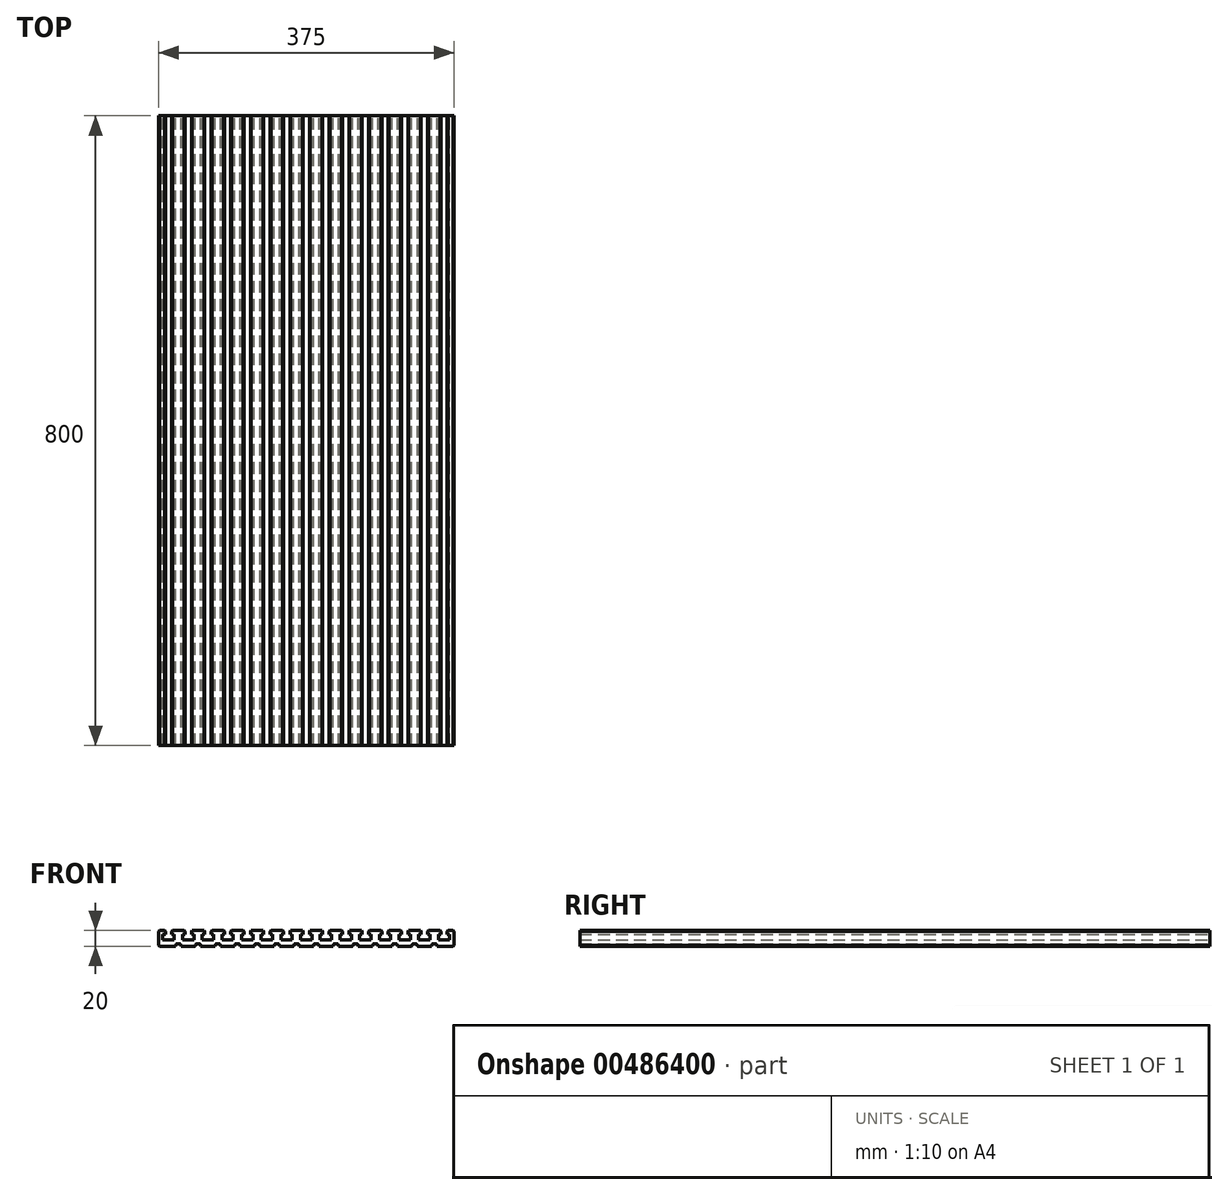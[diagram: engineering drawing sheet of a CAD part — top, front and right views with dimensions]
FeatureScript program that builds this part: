
annotation { "Feature Type Name" : "Feature", "Feature Type Description" : "" }
export const myFeature = defineFeature(function(context is Context, id is Id, definition is map)
    precondition{}
    {
        {
            var Q0;
            Q0=qCreatedBy(makeId("Front.planeOp"),FACE);
            var sketch = newSketch(context, id + "F0", { "sketchPlane" : qUnion([Q0])});
            skLineSegment(sketch, "E0", {"start": v(-186.5, -10) * mm, "end": v(-187.5, -9) * mm});
            skLineSegment(sketch, "E1", {"start": v(-187.5, -9) * mm, "end": v(-187.5, 9) * mm});
            skLineSegment(sketch, "E2", {"start": v(-187.5, 9) * mm, "end": v(-186.5, 10) * mm});
            skLineSegment(sketch, "E3", {"start": v(-186.5, 10) * mm, "end": v(-180.05, 10) * mm});
            skLineSegment(sketch, "E4", {"start": v(-179.05, 9) * mm, "end": v(-180.05, 10) * mm});
            skLineSegment(sketch, "E5", {"start": v(-179.05, 5) * mm, "end": v(-179.05, 9) * mm});
            skLineSegment(sketch, "E6", {"start": v(-182.25, 5) * mm, "end": v(-179.05, 5) * mm});
            skLineSegment(sketch, "E7", {"start": v(-182.25, -2) * mm, "end": v(-182.25, 5) * mm});
            skLineSegment(sketch, "E8", {"start": v(-167.75, -2) * mm, "end": v(-182.25, -2) * mm});
            skLineSegment(sketch, "E9", {"start": v(-167.75, 5) * mm, "end": v(-167.75, -2) * mm});
            skLineSegment(sketch, "E10", {"start": v(-170.95, 5) * mm, "end": v(-167.75, 5) * mm});
            skLineSegment(sketch, "E11", {"start": v(-170.95, 9) * mm, "end": v(-170.95, 5) * mm});
            skLineSegment(sketch, "E12", {"start": v(-169.95, 10) * mm, "end": v(-170.95, 9) * mm});
            skLineSegment(sketch, "E13", {"start": v(-169.95, 10) * mm, "end": v(-155.05, 10) * mm});
            skLineSegment(sketch, "E14", {"start": v(-154.05, 9) * mm, "end": v(-155.05, 10) * mm});
            skLineSegment(sketch, "E15", {"start": v(-154.05, 5) * mm, "end": v(-154.05, 9) * mm});
            skLineSegment(sketch, "E16", {"start": v(-157.25, 5) * mm, "end": v(-154.05, 5) * mm});
            skLineSegment(sketch, "E17", {"start": v(-157.25, -2) * mm, "end": v(-157.25, 5) * mm});
            skLineSegment(sketch, "E18", {"start": v(-142.75, -2) * mm, "end": v(-157.25, -2) * mm});
            skLineSegment(sketch, "E19", {"start": v(-142.75, 5) * mm, "end": v(-142.75, -2) * mm});
            skLineSegment(sketch, "E20", {"start": v(-145.95, 5) * mm, "end": v(-142.75, 5) * mm});
            skLineSegment(sketch, "E21", {"start": v(-145.95, 9) * mm, "end": v(-145.95, 5) * mm});
            skLineSegment(sketch, "E22", {"start": v(-144.95, 10) * mm, "end": v(-145.95, 9) * mm});
            skLineSegment(sketch, "E23", {"start": v(-144.95, 10) * mm, "end": v(-130.05, 10) * mm});
            skLineSegment(sketch, "E24", {"start": v(-129.05, 9) * mm, "end": v(-130.05, 10) * mm});
            skLineSegment(sketch, "E25", {"start": v(-129.05, 5) * mm, "end": v(-129.05, 9) * mm});
            skLineSegment(sketch, "E26", {"start": v(-132.25, 5) * mm, "end": v(-129.05, 5) * mm});
            skLineSegment(sketch, "E27", {"start": v(-132.25, -2) * mm, "end": v(-132.25, 5) * mm});
            skLineSegment(sketch, "E28", {"start": v(-117.75, -2) * mm, "end": v(-132.25, -2) * mm});
            skLineSegment(sketch, "E29", {"start": v(-117.75, 5) * mm, "end": v(-117.75, -2) * mm});
            skLineSegment(sketch, "E30", {"start": v(-120.95, 5) * mm, "end": v(-117.75, 5) * mm});
            skLineSegment(sketch, "E31", {"start": v(-120.95, 9) * mm, "end": v(-120.95, 5) * mm});
            skLineSegment(sketch, "E32", {"start": v(-119.95, 10) * mm, "end": v(-120.95, 9) * mm});
            skLineSegment(sketch, "E33", {"start": v(-119.95, 10) * mm, "end": v(-105.05, 10) * mm});
            skLineSegment(sketch, "E34", {"start": v(-104.05, 9) * mm, "end": v(-105.05, 10) * mm});
            skLineSegment(sketch, "E35", {"start": v(-104.05, 5) * mm, "end": v(-104.05, 9) * mm});
            skLineSegment(sketch, "E36", {"start": v(-107.25, 5) * mm, "end": v(-104.05, 5) * mm});
            skLineSegment(sketch, "E37", {"start": v(-107.25, -2) * mm, "end": v(-107.25, 5) * mm});
            skLineSegment(sketch, "E38", {"start": v(-92.75, -2) * mm, "end": v(-107.25, -2) * mm});
            skLineSegment(sketch, "E39", {"start": v(-92.75, 5) * mm, "end": v(-92.75, -2) * mm});
            skLineSegment(sketch, "E40", {"start": v(-95.95, 5) * mm, "end": v(-92.75, 5) * mm});
            skLineSegment(sketch, "E41", {"start": v(-95.95, 9) * mm, "end": v(-95.95, 5) * mm});
            skLineSegment(sketch, "E42", {"start": v(-94.95, 10) * mm, "end": v(-95.95, 9) * mm});
            skLineSegment(sketch, "E43", {"start": v(-94.95, 10) * mm, "end": v(-80.05, 10) * mm});
            skLineSegment(sketch, "E44", {"start": v(-79.05, 9) * mm, "end": v(-80.05, 10) * mm});
            skLineSegment(sketch, "E45", {"start": v(-79.05, 5) * mm, "end": v(-79.05, 9) * mm});
            skLineSegment(sketch, "E46", {"start": v(-82.25, 5) * mm, "end": v(-79.05, 5) * mm});
            skLineSegment(sketch, "E47", {"start": v(-82.25, -2) * mm, "end": v(-82.25, 5) * mm});
            skLineSegment(sketch, "E48", {"start": v(-67.75, -2) * mm, "end": v(-82.25, -2) * mm});
            skLineSegment(sketch, "E49", {"start": v(-67.75, 5) * mm, "end": v(-67.75, -2) * mm});
            skLineSegment(sketch, "E50", {"start": v(-70.95, 5) * mm, "end": v(-67.75, 5) * mm});
            skLineSegment(sketch, "E51", {"start": v(-70.95, 9) * mm, "end": v(-70.95, 5) * mm});
            skLineSegment(sketch, "E52", {"start": v(-69.95, 10) * mm, "end": v(-70.95, 9) * mm});
            skLineSegment(sketch, "E53", {"start": v(-69.95, 10) * mm, "end": v(-55.05, 10) * mm});
            skLineSegment(sketch, "E54", {"start": v(-54.05, 9) * mm, "end": v(-55.05, 10) * mm});
            skLineSegment(sketch, "E55", {"start": v(-54.05, 5) * mm, "end": v(-54.05, 9) * mm});
            skLineSegment(sketch, "E56", {"start": v(-57.25, 5) * mm, "end": v(-54.05, 5) * mm});
            skLineSegment(sketch, "E57", {"start": v(-57.25, -2) * mm, "end": v(-57.25, 5) * mm});
            skLineSegment(sketch, "E58", {"start": v(-42.75, -2) * mm, "end": v(-57.25, -2) * mm});
            skLineSegment(sketch, "E59", {"start": v(-42.75, 5) * mm, "end": v(-42.75, -2) * mm});
            skLineSegment(sketch, "E60", {"start": v(-45.95, 5) * mm, "end": v(-42.75, 5) * mm});
            skLineSegment(sketch, "E61", {"start": v(-45.95, 9) * mm, "end": v(-45.95, 5) * mm});
            skLineSegment(sketch, "E62", {"start": v(-44.95, 10) * mm, "end": v(-45.95, 9) * mm});
            skLineSegment(sketch, "E63", {"start": v(-44.95, 10) * mm, "end": v(-30.05, 10) * mm});
            skLineSegment(sketch, "E64", {"start": v(-29.05, 9) * mm, "end": v(-30.05, 10) * mm});
            skLineSegment(sketch, "E65", {"start": v(-32.25, 5) * mm, "end": v(-29.05, 5) * mm});
            skLineSegment(sketch, "E66", {"start": v(-32.25, -2) * mm, "end": v(-32.25, 5) * mm});
            skLineSegment(sketch, "E67", {"start": v(-17.75, -2) * mm, "end": v(-32.25, -2) * mm});
            skLineSegment(sketch, "E68", {"start": v(-17.75, 5) * mm, "end": v(-17.75, -2) * mm});
            skLineSegment(sketch, "E69", {"start": v(-20.95, 5) * mm, "end": v(-17.75, 5) * mm});
            skLineSegment(sketch, "E70", {"start": v(-20.95, 9) * mm, "end": v(-20.95, 5) * mm});
            skLineSegment(sketch, "E71", {"start": v(-19.95, 10) * mm, "end": v(-20.95, 9) * mm});
            skLineSegment(sketch, "E72", {"start": v(-19.95, 10) * mm, "end": v(-5.05, 10) * mm});
            skLineSegment(sketch, "E73", {"start": v(-4.05, 9) * mm, "end": v(-5.05, 10) * mm});
            skLineSegment(sketch, "E74", {"start": v(-4.05, 5) * mm, "end": v(-4.05, 9) * mm});
            skLineSegment(sketch, "E75", {"start": v(-7.25, 5) * mm, "end": v(-4.05, 5) * mm});
            skLineSegment(sketch, "E76", {"start": v(-7.25, -2) * mm, "end": v(-7.25, 5) * mm});
            skLineSegment(sketch, "E77", {"start": v(7.25, -2) * mm, "end": v(-7.25, -2) * mm});
            skLineSegment(sketch, "E78", {"start": v(7.25, -2) * mm, "end": v(7.25, 5) * mm});
            skLineSegment(sketch, "E79", {"start": v(7.25, 5) * mm, "end": v(4.05, 5) * mm});
            skLineSegment(sketch, "E80", {"start": v(4.05, 5) * mm, "end": v(4.05, 9) * mm});
            skLineSegment(sketch, "E81", {"start": v(4.05, 9) * mm, "end": v(5.05, 10) * mm});
            skLineSegment(sketch, "E82", {"start": v(19.95, 10) * mm, "end": v(20.95, 9) * mm});
            skLineSegment(sketch, "E83", {"start": v(20.95, 9) * mm, "end": v(20.95, 5) * mm});
            skLineSegment(sketch, "E84", {"start": v(20.95, 5) * mm, "end": v(17.75, 5) * mm});
            skLineSegment(sketch, "E85", {"start": v(17.75, 5) * mm, "end": v(17.75, -2) * mm});
            skLineSegment(sketch, "E86", {"start": v(17.75, -2) * mm, "end": v(32.25, -2) * mm});
            skLineSegment(sketch, "E87", {"start": v(32.25, -2) * mm, "end": v(32.25, 5) * mm});
            skLineSegment(sketch, "E88", {"start": v(32.25, 5) * mm, "end": v(29.05, 5) * mm});
            skLineSegment(sketch, "E89", {"start": v(29.05, 5) * mm, "end": v(29.05, 9) * mm});
            skLineSegment(sketch, "E90", {"start": v(29.05, 9) * mm, "end": v(30.05, 10) * mm});
            skLineSegment(sketch, "E91", {"start": v(44.95, 10) * mm, "end": v(45.95, 9) * mm});
            skLineSegment(sketch, "E92", {"start": v(45.95, 9) * mm, "end": v(45.95, 5) * mm});
            skLineSegment(sketch, "E93", {"start": v(45.95, 5) * mm, "end": v(42.75, 5) * mm});
            skLineSegment(sketch, "E94", {"start": v(42.75, 5) * mm, "end": v(42.75, -2) * mm});
            skLineSegment(sketch, "E95", {"start": v(42.75, -2) * mm, "end": v(57.25, -2) * mm});
            skLineSegment(sketch, "E96", {"start": v(57.25, -2) * mm, "end": v(57.25, 5) * mm});
            skLineSegment(sketch, "E97", {"start": v(57.25, 5) * mm, "end": v(54.05, 5) * mm});
            skLineSegment(sketch, "E98", {"start": v(54.05, 5) * mm, "end": v(54.05, 9) * mm});
            skLineSegment(sketch, "E99", {"start": v(54.05, 9) * mm, "end": v(55.05, 10) * mm});
            skLineSegment(sketch, "E100", {"start": v(69.95, 10) * mm, "end": v(70.95, 9) * mm});
            skLineSegment(sketch, "E101", {"start": v(70.95, 9) * mm, "end": v(70.95, 5) * mm});
            skLineSegment(sketch, "E102", {"start": v(70.95, 5) * mm, "end": v(67.75, 5) * mm});
            skLineSegment(sketch, "E103", {"start": v(67.75, 5) * mm, "end": v(67.75, -2) * mm});
            skLineSegment(sketch, "E104", {"start": v(67.75, -2) * mm, "end": v(82.25, -2) * mm});
            skLineSegment(sketch, "E105", {"start": v(82.25, -2) * mm, "end": v(82.25, 5) * mm});
            skLineSegment(sketch, "E106", {"start": v(82.25, 5) * mm, "end": v(79.05, 5) * mm});
            skLineSegment(sketch, "E107", {"start": v(79.05, 5) * mm, "end": v(79.05, 9) * mm});
            skLineSegment(sketch, "E108", {"start": v(79.05, 9) * mm, "end": v(80.05, 10) * mm});
            skLineSegment(sketch, "E109", {"start": v(94.95, 10) * mm, "end": v(95.95, 9) * mm});
            skLineSegment(sketch, "E110", {"start": v(95.95, 9) * mm, "end": v(95.95, 5) * mm});
            skLineSegment(sketch, "E111", {"start": v(95.95, 5) * mm, "end": v(92.75, 5) * mm});
            skLineSegment(sketch, "E112", {"start": v(92.75, 5) * mm, "end": v(92.75, -2) * mm});
            skLineSegment(sketch, "E113", {"start": v(92.75, -2) * mm, "end": v(107.25, -2) * mm});
            skLineSegment(sketch, "E114", {"start": v(107.25, -2) * mm, "end": v(107.25, 5) * mm});
            skLineSegment(sketch, "E115", {"start": v(107.25, 5) * mm, "end": v(104.05, 5) * mm});
            skLineSegment(sketch, "E116", {"start": v(104.05, 5) * mm, "end": v(104.05, 9) * mm});
            skLineSegment(sketch, "E117", {"start": v(104.05, 9) * mm, "end": v(105.05, 10) * mm});
            skLineSegment(sketch, "E118", {"start": v(119.95, 10) * mm, "end": v(120.95, 9) * mm});
            skLineSegment(sketch, "E119", {"start": v(120.95, 9) * mm, "end": v(120.95, 5) * mm});
            skLineSegment(sketch, "E120", {"start": v(120.95, 5) * mm, "end": v(117.75, 5) * mm});
            skLineSegment(sketch, "E121", {"start": v(117.75, 5) * mm, "end": v(117.75, -2) * mm});
            skLineSegment(sketch, "E122", {"start": v(117.75, -2) * mm, "end": v(132.25, -2) * mm});
            skLineSegment(sketch, "E123", {"start": v(132.25, -2) * mm, "end": v(132.25, 5) * mm});
            skLineSegment(sketch, "E124", {"start": v(132.25, 5) * mm, "end": v(129.05, 5) * mm});
            skLineSegment(sketch, "E125", {"start": v(129.05, 5) * mm, "end": v(129.05, 9) * mm});
            skLineSegment(sketch, "E126", {"start": v(129.05, 9) * mm, "end": v(130.05, 10) * mm});
            skLineSegment(sketch, "E127", {"start": v(144.95, 10) * mm, "end": v(145.95, 9) * mm});
            skLineSegment(sketch, "E128", {"start": v(145.95, 9) * mm, "end": v(145.95, 5) * mm});
            skLineSegment(sketch, "E129", {"start": v(145.95, 5) * mm, "end": v(142.75, 5) * mm});
            skLineSegment(sketch, "E130", {"start": v(142.75, 5) * mm, "end": v(142.75, -2) * mm});
            skLineSegment(sketch, "E131", {"start": v(142.75, -2) * mm, "end": v(157.25, -2) * mm});
            skLineSegment(sketch, "E132", {"start": v(157.25, -2) * mm, "end": v(157.25, 5) * mm});
            skLineSegment(sketch, "E133", {"start": v(157.25, 5) * mm, "end": v(154.05, 5) * mm});
            skLineSegment(sketch, "E134", {"start": v(154.05, 5) * mm, "end": v(154.05, 9) * mm});
            skLineSegment(sketch, "E135", {"start": v(154.05, 9) * mm, "end": v(155.05, 10) * mm});
            skLineSegment(sketch, "E136", {"start": v(169.95, 10) * mm, "end": v(170.95, 9) * mm});
            skLineSegment(sketch, "E137", {"start": v(170.95, 9) * mm, "end": v(170.95, 5) * mm});
            skLineSegment(sketch, "E138", {"start": v(170.95, 5) * mm, "end": v(167.75, 5) * mm});
            skLineSegment(sketch, "E139", {"start": v(167.75, 5) * mm, "end": v(167.75, -2) * mm});
            skLineSegment(sketch, "E140", {"start": v(167.75, -2) * mm, "end": v(182.25, -2) * mm});
            skLineSegment(sketch, "E141", {"start": v(182.25, -2) * mm, "end": v(182.25, 5) * mm});
            skLineSegment(sketch, "E142", {"start": v(182.25, 5) * mm, "end": v(179.05, 5) * mm});
            skLineSegment(sketch, "E143", {"start": v(179.05, 5) * mm, "end": v(179.05, 9) * mm});
            skLineSegment(sketch, "E144", {"start": v(179.05, 9) * mm, "end": v(180.05, 10) * mm});
            skArc(sketch, "E145", {"start": v(165.87, -9.56) * mm, "mid": v(165.94, -9.79) * mm, "end": v(166.04, -10) * mm});
            skLineSegment(sketch, "E146", {"start": v(165.87, -9.56) * mm, "end": v(165.53, -7.94) * mm});
            skArc(sketch, "E147", {"start": v(165.53, -7.94) * mm, "mid": v(165, -7.08) * mm, "end": v(164.06, -6.75) * mm});
            skLineSegment(sketch, "E148", {"start": v(164.06, -6.75) * mm, "end": v(160.94, -6.75) * mm});
            skArc(sketch, "E149", {"start": v(160.94, -6.75) * mm, "mid": v(160, -7.08) * mm, "end": v(159.47, -7.94) * mm});
            skLineSegment(sketch, "E150", {"start": v(159.47, -7.94) * mm, "end": v(159.13, -9.56) * mm});
            skArc(sketch, "E151", {"start": v(158.96, -10) * mm, "mid": v(159.06, -9.79) * mm, "end": v(159.13, -9.56) * mm});
            skArc(sketch, "E152", {"start": v(140.87, -9.56) * mm, "mid": v(140.94, -9.79) * mm, "end": v(141.04, -10) * mm});
            skLineSegment(sketch, "E153", {"start": v(140.87, -9.56) * mm, "end": v(140.53, -7.94) * mm});
            skArc(sketch, "E154", {"start": v(140.53, -7.94) * mm, "mid": v(140, -7.08) * mm, "end": v(139.06, -6.75) * mm});
            skLineSegment(sketch, "E155", {"start": v(139.06, -6.75) * mm, "end": v(135.94, -6.75) * mm});
            skArc(sketch, "E156", {"start": v(135.94, -6.75) * mm, "mid": v(135, -7.08) * mm, "end": v(134.47, -7.94) * mm});
            skLineSegment(sketch, "E157", {"start": v(134.47, -7.94) * mm, "end": v(134.13, -9.56) * mm});
            skArc(sketch, "E158", {"start": v(133.96, -10) * mm, "mid": v(134.06, -9.79) * mm, "end": v(134.13, -9.56) * mm});
            skArc(sketch, "E159", {"start": v(115.87, -9.56) * mm, "mid": v(115.94, -9.79) * mm, "end": v(116.04, -10) * mm});
            skLineSegment(sketch, "E160", {"start": v(115.87, -9.56) * mm, "end": v(115.53, -7.94) * mm});
            skArc(sketch, "E161", {"start": v(115.53, -7.94) * mm, "mid": v(115, -7.08) * mm, "end": v(114.06, -6.75) * mm});
            skLineSegment(sketch, "E162", {"start": v(114.06, -6.75) * mm, "end": v(110.94, -6.75) * mm});
            skArc(sketch, "E163", {"start": v(110.94, -6.75) * mm, "mid": v(110, -7.08) * mm, "end": v(109.47, -7.94) * mm});
            skLineSegment(sketch, "E164", {"start": v(109.47, -7.94) * mm, "end": v(109.13, -9.56) * mm});
            skArc(sketch, "E165", {"start": v(108.96, -10) * mm, "mid": v(109.06, -9.79) * mm, "end": v(109.13, -9.56) * mm});
            skArc(sketch, "E166", {"start": v(90.87, -9.56) * mm, "mid": v(90.94, -9.79) * mm, "end": v(91.04, -10) * mm});
            skLineSegment(sketch, "E167", {"start": v(90.87, -9.56) * mm, "end": v(90.53, -7.94) * mm});
            skArc(sketch, "E168", {"start": v(90.53, -7.94) * mm, "mid": v(90, -7.08) * mm, "end": v(89.06, -6.75) * mm});
            skLineSegment(sketch, "E169", {"start": v(89.06, -6.75) * mm, "end": v(85.94, -6.75) * mm});
            skArc(sketch, "E170", {"start": v(85.94, -6.75) * mm, "mid": v(85, -7.08) * mm, "end": v(84.47, -7.94) * mm});
            skLineSegment(sketch, "E171", {"start": v(84.47, -7.94) * mm, "end": v(84.13, -9.56) * mm});
            skArc(sketch, "E172", {"start": v(83.96, -10) * mm, "mid": v(84.06, -9.79) * mm, "end": v(84.13, -9.56) * mm});
            skArc(sketch, "E173", {"start": v(65.87, -9.56) * mm, "mid": v(65.94, -9.79) * mm, "end": v(66.04, -10) * mm});
            skLineSegment(sketch, "E174", {"start": v(65.87, -9.56) * mm, "end": v(65.53, -7.94) * mm});
            skArc(sketch, "E175", {"start": v(65.53, -7.94) * mm, "mid": v(65, -7.08) * mm, "end": v(64.06, -6.75) * mm});
            skLineSegment(sketch, "E176", {"start": v(64.06, -6.75) * mm, "end": v(60.94, -6.75) * mm});
            skArc(sketch, "E177", {"start": v(60.94, -6.75) * mm, "mid": v(60, -7.08) * mm, "end": v(59.47, -7.94) * mm});
            skLineSegment(sketch, "E178", {"start": v(59.47, -7.94) * mm, "end": v(59.13, -9.56) * mm});
            skArc(sketch, "E179", {"start": v(58.96, -10) * mm, "mid": v(59.06, -9.79) * mm, "end": v(59.13, -9.56) * mm});
            skArc(sketch, "E180", {"start": v(40.87, -9.56) * mm, "mid": v(40.94, -9.79) * mm, "end": v(41.04, -10) * mm});
            skLineSegment(sketch, "E181", {"start": v(40.87, -9.56) * mm, "end": v(40.53, -7.94) * mm});
            skArc(sketch, "E182", {"start": v(40.53, -7.94) * mm, "mid": v(40, -7.08) * mm, "end": v(39.06, -6.75) * mm});
            skLineSegment(sketch, "E183", {"start": v(39.06, -6.75) * mm, "end": v(35.94, -6.75) * mm});
            skArc(sketch, "E184", {"start": v(35.94, -6.75) * mm, "mid": v(35, -7.08) * mm, "end": v(34.47, -7.94) * mm});
            skLineSegment(sketch, "E185", {"start": v(34.47, -7.94) * mm, "end": v(34.13, -9.56) * mm});
            skArc(sketch, "E186", {"start": v(33.96, -10) * mm, "mid": v(34.06, -9.79) * mm, "end": v(34.13, -9.56) * mm});
            skArc(sketch, "E187", {"start": v(15.87, -9.56) * mm, "mid": v(15.94, -9.79) * mm, "end": v(16.04, -10) * mm});
            skLineSegment(sketch, "E188", {"start": v(15.87, -9.56) * mm, "end": v(15.53, -7.94) * mm});
            skArc(sketch, "E189", {"start": v(15.53, -7.94) * mm, "mid": v(15, -7.08) * mm, "end": v(14.06, -6.75) * mm});
            skLineSegment(sketch, "E190", {"start": v(14.06, -6.75) * mm, "end": v(10.94, -6.75) * mm});
            skArc(sketch, "E191", {"start": v(10.94, -6.75) * mm, "mid": v(10, -7.08) * mm, "end": v(9.47, -7.94) * mm});
            skLineSegment(sketch, "E192", {"start": v(9.47, -7.94) * mm, "end": v(9.13, -9.56) * mm});
            skArc(sketch, "E193", {"start": v(8.96, -10) * mm, "mid": v(9.06, -9.79) * mm, "end": v(9.13, -9.56) * mm});
            skArc(sketch, "E194", {"start": v(-9.13, -9.56) * mm, "mid": v(-9.06, -9.79) * mm, "end": v(-8.96, -10) * mm});
            skLineSegment(sketch, "E195", {"start": v(-9.13, -9.56) * mm, "end": v(-9.47, -7.94) * mm});
            skArc(sketch, "E196", {"start": v(-9.47, -7.94) * mm, "mid": v(-10, -7.08) * mm, "end": v(-10.94, -6.75) * mm});
            skLineSegment(sketch, "E197", {"start": v(-10.94, -6.75) * mm, "end": v(-14.06, -6.75) * mm});
            skArc(sketch, "E198", {"start": v(-14.06, -6.75) * mm, "mid": v(-15, -7.08) * mm, "end": v(-15.53, -7.94) * mm});
            skLineSegment(sketch, "E199", {"start": v(-15.53, -7.94) * mm, "end": v(-15.87, -9.56) * mm});
            skArc(sketch, "E200", {"start": v(-16.04, -10) * mm, "mid": v(-15.94, -9.79) * mm, "end": v(-15.87, -9.56) * mm});
            skArc(sketch, "E201", {"start": v(-34.13, -9.56) * mm, "mid": v(-34.06, -9.79) * mm, "end": v(-33.96, -10) * mm});
            skLineSegment(sketch, "E202", {"start": v(-34.13, -9.56) * mm, "end": v(-34.47, -7.94) * mm});
            skArc(sketch, "E203", {"start": v(-34.47, -7.94) * mm, "mid": v(-35, -7.08) * mm, "end": v(-35.94, -6.75) * mm});
            skLineSegment(sketch, "E204", {"start": v(-35.94, -6.75) * mm, "end": v(-39.06, -6.75) * mm});
            skArc(sketch, "E205", {"start": v(-39.06, -6.75) * mm, "mid": v(-40, -7.08) * mm, "end": v(-40.53, -7.94) * mm});
            skLineSegment(sketch, "E206", {"start": v(-40.53, -7.94) * mm, "end": v(-40.87, -9.56) * mm});
            skArc(sketch, "E207", {"start": v(-41.04, -10) * mm, "mid": v(-40.94, -9.79) * mm, "end": v(-40.87, -9.56) * mm});
            skArc(sketch, "E208", {"start": v(-59.13, -9.56) * mm, "mid": v(-59.06, -9.79) * mm, "end": v(-58.96, -10) * mm});
            skLineSegment(sketch, "E209", {"start": v(-59.13, -9.56) * mm, "end": v(-59.47, -7.94) * mm});
            skArc(sketch, "E210", {"start": v(-59.47, -7.94) * mm, "mid": v(-60, -7.08) * mm, "end": v(-60.94, -6.75) * mm});
            skLineSegment(sketch, "E211", {"start": v(-60.94, -6.75) * mm, "end": v(-64.06, -6.75) * mm});
            skArc(sketch, "E212", {"start": v(-64.06, -6.75) * mm, "mid": v(-65, -7.08) * mm, "end": v(-65.53, -7.94) * mm});
            skLineSegment(sketch, "E213", {"start": v(-65.53, -7.94) * mm, "end": v(-65.87, -9.56) * mm});
            skArc(sketch, "E214", {"start": v(-66.04, -10) * mm, "mid": v(-65.94, -9.79) * mm, "end": v(-65.87, -9.56) * mm});
            skArc(sketch, "E215", {"start": v(-84.13, -9.56) * mm, "mid": v(-84.06, -9.79) * mm, "end": v(-83.96, -10) * mm});
            skLineSegment(sketch, "E216", {"start": v(-84.13, -9.56) * mm, "end": v(-84.47, -7.94) * mm});
            skArc(sketch, "E217", {"start": v(-84.47, -7.94) * mm, "mid": v(-85, -7.08) * mm, "end": v(-85.94, -6.75) * mm});
            skLineSegment(sketch, "E218", {"start": v(-85.94, -6.75) * mm, "end": v(-89.06, -6.75) * mm});
            skArc(sketch, "E219", {"start": v(-89.06, -6.75) * mm, "mid": v(-90, -7.08) * mm, "end": v(-90.53, -7.94) * mm});
            skLineSegment(sketch, "E220", {"start": v(-90.53, -7.94) * mm, "end": v(-90.87, -9.56) * mm});
            skArc(sketch, "E221", {"start": v(-91.04, -10) * mm, "mid": v(-90.94, -9.79) * mm, "end": v(-90.87, -9.56) * mm});
            skArc(sketch, "E222", {"start": v(-109.13, -9.56) * mm, "mid": v(-109.06, -9.79) * mm, "end": v(-108.96, -10) * mm});
            skLineSegment(sketch, "E223", {"start": v(-109.13, -9.56) * mm, "end": v(-109.47, -7.94) * mm});
            skArc(sketch, "E224", {"start": v(-109.47, -7.94) * mm, "mid": v(-110, -7.08) * mm, "end": v(-110.94, -6.75) * mm});
            skLineSegment(sketch, "E225", {"start": v(-110.94, -6.75) * mm, "end": v(-114.06, -6.75) * mm});
            skArc(sketch, "E226", {"start": v(-114.06, -6.75) * mm, "mid": v(-115, -7.08) * mm, "end": v(-115.53, -7.94) * mm});
            skLineSegment(sketch, "E227", {"start": v(-115.53, -7.94) * mm, "end": v(-115.87, -9.56) * mm});
            skArc(sketch, "E228", {"start": v(-116.04, -10) * mm, "mid": v(-115.94, -9.79) * mm, "end": v(-115.87, -9.56) * mm});
            skArc(sketch, "E229", {"start": v(-134.13, -9.56) * mm, "mid": v(-134.06, -9.79) * mm, "end": v(-133.96, -10) * mm});
            skLineSegment(sketch, "E230", {"start": v(-134.13, -9.56) * mm, "end": v(-134.47, -7.94) * mm});
            skArc(sketch, "E231", {"start": v(-134.47, -7.94) * mm, "mid": v(-135, -7.08) * mm, "end": v(-135.94, -6.75) * mm});
            skLineSegment(sketch, "E232", {"start": v(-135.94, -6.75) * mm, "end": v(-139.06, -6.75) * mm});
            skArc(sketch, "E233", {"start": v(-139.06, -6.75) * mm, "mid": v(-140, -7.08) * mm, "end": v(-140.53, -7.94) * mm});
            skLineSegment(sketch, "E234", {"start": v(-140.53, -7.94) * mm, "end": v(-140.87, -9.56) * mm});
            skArc(sketch, "E235", {"start": v(-141.04, -10) * mm, "mid": v(-140.94, -9.79) * mm, "end": v(-140.87, -9.56) * mm});
            skArc(sketch, "E236", {"start": v(-159.13, -9.56) * mm, "mid": v(-159.06, -9.79) * mm, "end": v(-158.96, -10) * mm});
            skLineSegment(sketch, "E237", {"start": v(-159.13, -9.56) * mm, "end": v(-159.47, -7.94) * mm});
            skArc(sketch, "E238", {"start": v(-159.47, -7.94) * mm, "mid": v(-160, -7.08) * mm, "end": v(-160.94, -6.75) * mm});
            skLineSegment(sketch, "E239", {"start": v(-160.94, -6.75) * mm, "end": v(-164.06, -6.75) * mm});
            skArc(sketch, "E240", {"start": v(-164.06, -6.75) * mm, "mid": v(-165, -7.08) * mm, "end": v(-165.53, -7.94) * mm});
            skLineSegment(sketch, "E241", {"start": v(-165.53, -7.94) * mm, "end": v(-165.87, -9.56) * mm});
            skArc(sketch, "E242", {"start": v(-166.04, -10) * mm, "mid": v(-165.94, -9.79) * mm, "end": v(-165.87, -9.56) * mm});
            skLineSegment(sketch, "E243", {"start": v(-29.05, 5) * mm, "end": v(-29.05, 9) * mm});
            skLineSegment(sketch, "E244", {"start": v(166.04, -10) * mm, "end": v(186.5, -10) * mm});
            skLineSegment(sketch, "E245", {"start": v(186.5, -10) * mm, "end": v(187.5, -9) * mm});
            skLineSegment(sketch, "E246", {"start": v(187.5, -9) * mm, "end": v(187.5, 9) * mm});
            skLineSegment(sketch, "E247", {"start": v(187.5, 9) * mm, "end": v(186.5, 10) * mm});
            skLineSegment(sketch, "E248", {"start": v(19.95, 10) * mm, "end": v(5.05, 10) * mm});
            skLineSegment(sketch, "E249", {"start": v(186.5, 10) * mm, "end": v(180.05, 10) * mm});
            skLineSegment(sketch, "E250", {"start": v(169.95, 10) * mm, "end": v(155.05, 10) * mm});
            skLineSegment(sketch, "E251", {"start": v(144.95, 10) * mm, "end": v(130.05, 10) * mm});
            skLineSegment(sketch, "E252", {"start": v(119.95, 10) * mm, "end": v(105.05, 10) * mm});
            skLineSegment(sketch, "E253", {"start": v(94.95, 10) * mm, "end": v(80.05, 10) * mm});
            skLineSegment(sketch, "E254", {"start": v(69.95, 10) * mm, "end": v(55.05, 10) * mm});
            skLineSegment(sketch, "E255", {"start": v(44.95, 10) * mm, "end": v(30.05, 10) * mm});
            skLineSegment(sketch, "E256", {"start": v(141.04, -10) * mm, "end": v(158.96, -10) * mm});
            skLineSegment(sketch, "E257", {"start": v(116.04, -10) * mm, "end": v(133.96, -10) * mm});
            skLineSegment(sketch, "E258", {"start": v(91.04, -10) * mm, "end": v(108.96, -10) * mm});
            skLineSegment(sketch, "E259", {"start": v(66.04, -10) * mm, "end": v(83.96, -10) * mm});
            skLineSegment(sketch, "E260", {"start": v(41.04, -10) * mm, "end": v(58.96, -10) * mm});
            skLineSegment(sketch, "E261", {"start": v(16.04, -10) * mm, "end": v(33.96, -10) * mm});
            skLineSegment(sketch, "E262", {"start": v(-8.96, -10) * mm, "end": v(8.96, -10) * mm});
            skLineSegment(sketch, "E263", {"start": v(-33.96, -10) * mm, "end": v(-16.04, -10) * mm});
            skLineSegment(sketch, "E264", {"start": v(-58.96, -10) * mm, "end": v(-41.04, -10) * mm});
            skLineSegment(sketch, "E265", {"start": v(-83.96, -10) * mm, "end": v(-66.04, -10) * mm});
            skLineSegment(sketch, "E266", {"start": v(-108.96, -10) * mm, "end": v(-91.04, -10) * mm});
            skLineSegment(sketch, "E267", {"start": v(-133.96, -10) * mm, "end": v(-116.04, -10) * mm});
            skLineSegment(sketch, "E268", {"start": v(-158.96, -10) * mm, "end": v(-141.04, -10) * mm});
            skLineSegment(sketch, "E269", {"start": v(-186.5, -10) * mm, "end": v(-166.04, -10) * mm});
            skSolve(sketch);
        }
        {
            var Q0;
            Q0 = qSketchRegion(id + "F0", true);
            extrude(context, id + "F1", {"entities" : qUnion([Q0]), "depth" : 800 * mm});
        }
    });
